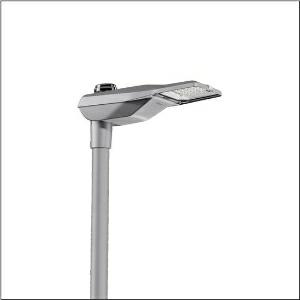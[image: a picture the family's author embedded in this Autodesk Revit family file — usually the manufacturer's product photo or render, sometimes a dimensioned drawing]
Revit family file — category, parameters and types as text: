
# Revit family: streetlight_sl_21_micro___st1_5a_5xe5p47n08db_8f26
name_source: partatom
category: Lighting Fixtures
units: mm (PartAtom-declared; Revit-internal decimal feet)

## family parameters
Cut with Voids When Loaded = No
Host = Face
Light Source = No
Part Type = Normal
Room Calculation Point = No
Round Connector Dimension = Use Diameter
Shared = No

## types (1)
- --- (1 x LED, 5230 lm, 39.1 W, 4000K)
    Apparent Load = 39 VA
    CIE Flux Codes = 22 53 95 100 100
    Color Rendering = 70
    Color Temperature = 4000K
    Default Elevation = 1800 mm
    Description = Streetlight SL 21 micro, mast luminaire, primary light control with lens, of PMMA, primary optical cover: cover, of toughened safety glass, transparent, light distribution: ST1.5a, light emission: direct distribution, primary light characteristic: asymmetric, installation type: post-top, LED, 3G 1.5mm², High Power LED, rated luminous flux: 5.230lm, luminous efficacy: 134lm/W, light colour: 740, colour temperature: 4000K, control gear: NEMA (7pin), control: overheat protection, pre-setting: linear dimming characteristic, constant luminous flux control, time-dependent luminous flux control, flexible luminous flux parameterisation, mains connection: 230..240V, AC, 50/60Hz, connection cable pre-assembled, cable length: 6,5m, wiring characteristics: H07RN-F, start of lifetime: 39W, end of service life: 41W, reduction: 18W, luminaire housing, of diecast aluminium (EN AC-44300), powder-coated, SITECO metallic grey (DB 702S), corrosivity category C5 high according to DIN EN ISO 12944, multi-level sealing system, sealing non-destructively replaceable, inclination adjustable: 0°, 5°, 10°, 15°, length: 528mm, width: 235mm, height: 110mm, spigot size: 76/60mm (post-top), mounting height: 4..8m, protection rating (complete): IP66, insulation class (complete): insulation class I (protective earthing), certification: CE, ENEC, ENEC+, VDE, impact resistance: IK10, permissible operating ambient temperature for outdoor applications: -40..+50°C, standard-compliant lighting for roads and squares, packaging unit: 1 piece

Light Distribution: ST1.5a
    Height = 110 mm
    Lamp = 1 x LED
    Lamp Light Flux = 5230 lm
    Lamp Power = 39.1 W
    Lamp count = 1
    Length = 528 mm
    Luminous efficacy = 134 lm/W
    Manufacturer = Siteco
    ModVariant = No
    Model = 5XE5P47N08DB
    Number of Poles = 1
    OnlyDefault = Yes
    Power Factor = 1
    Product Name = Streetlight SL 21 micro | ST1.5a
    Product group = mast luminaire | pylon top
    ProductGroupID = 6100
    Protection Class = Protection class I
    Protection Degree = IP 66
    RLX_Detail_Level = 1
    RLX_Emergency_Light_Flux = 0 lm
    RLX_Emergency_Type = 0
    RLX_Emergency_Type_DB = No
    RlxData = <blob elided: 102897 chars, md5=d7a11293>
    Socket = socket
    Standby Power = 0 W
    System Light Flux = 5230 lm
    System Power = 39 W
    Type Comments = factory setting: luminous flux: 100 % | dim-lin: 254 | 765 mA
    Type Image = l_1294375.jpg
    URL = http://relux.com
    VarID = @adj_133191
    Voltage = 0 V
    Weight = 0.00 kg
    Width = 235 mm

## geometry (parser evidence)
native form markers: Blend x4, Sweep x10
no freeform markers — native parametric forms only
